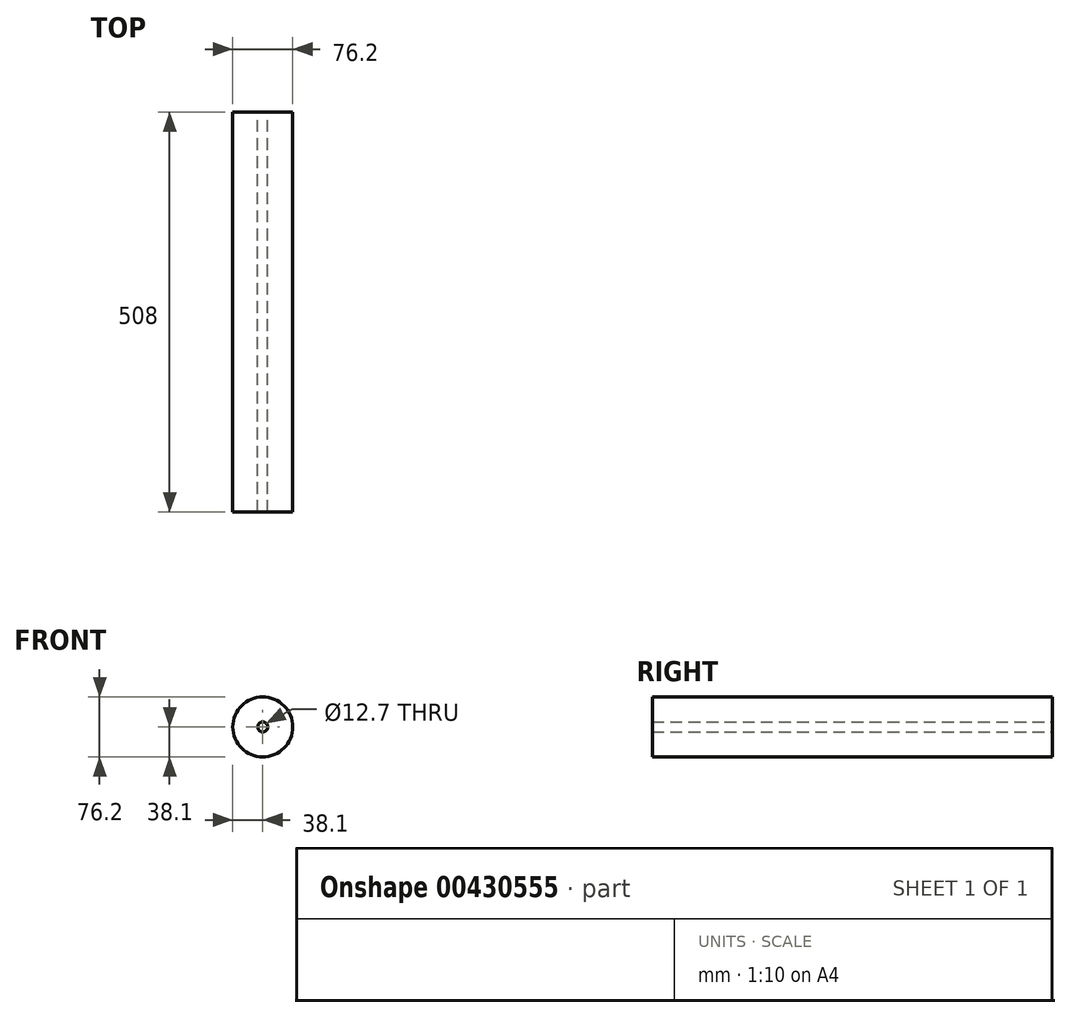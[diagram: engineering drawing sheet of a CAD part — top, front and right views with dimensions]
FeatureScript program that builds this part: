
annotation { "Feature Type Name" : "Feature", "Feature Type Description" : "" }
export const myFeature = defineFeature(function(context is Context, id is Id, definition is map)
    precondition{}
    {
        {
            var Q0;
            Q0=qCreatedBy(makeId("Front.planeOp"),FACE);
            var sketch = newSketch(context, id + "F0", { "sketchPlane" : qUnion([Q0])});
            skCircle(sketch, "E0", {"center": v(0, 0) * mm, "radius": 38.1 * mm});
            skCircle(sketch, "E1", {"center": v(0, 0) * mm, "radius": 6.35 * mm});
            skSolve(sketch);
        }
        {
            var Q0;
            Q0=makeQuery(id+"F0.imprint","IMPRINT",FACE,{"disambiguationData":[TD([[makeQuery(id+"F0.imprint","IMPRINT",EDGE,{"derivedFrom":sQuery(id+"F0.wireOp",EDGE,"E0")}),1.0]])]});
            extrude(context, id + "F1", {"entities" : qUnion([Q0]), "depth" : 508 * mm});
        }
    });
